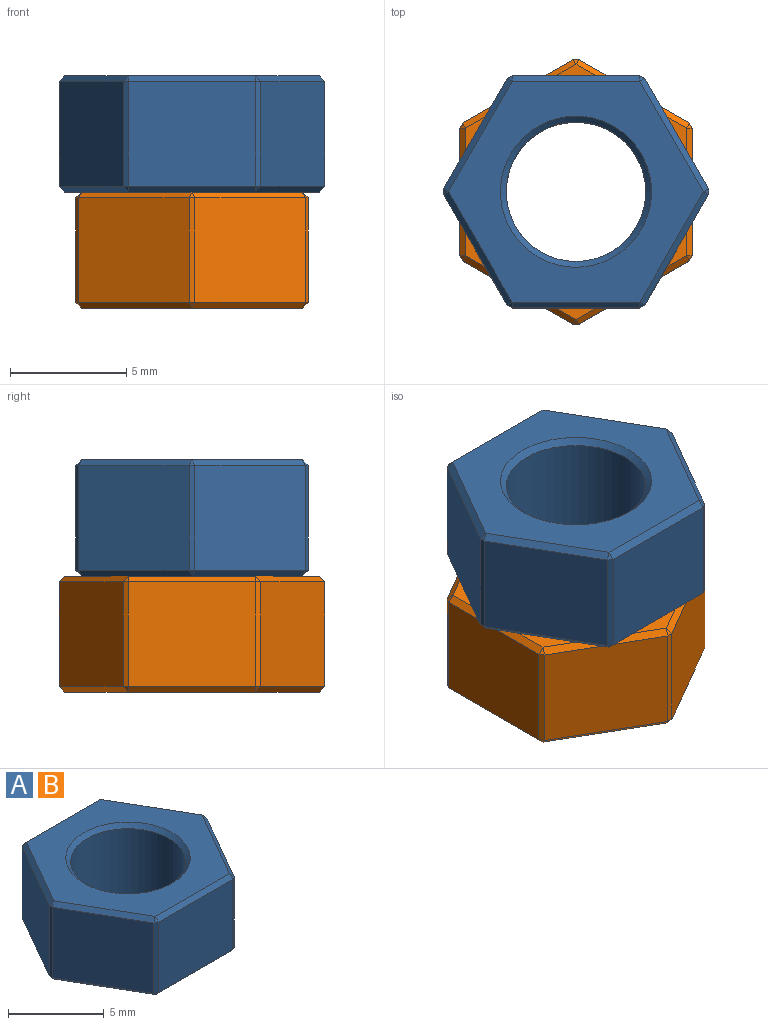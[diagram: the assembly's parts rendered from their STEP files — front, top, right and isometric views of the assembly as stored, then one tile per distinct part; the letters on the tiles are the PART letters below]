
ASSEMBLY  parts=2 mates=1
PART A: 40 faces, bbox 11.4x10x5 mm
  f0: plane 4.75x4.5mm, normal (-0.87,-0.5,0), area 24.7mm2, adj f15,f24,f25,f26
  f1: plane 5.49x4.5mm, normal (0,-1,0), area 24.7mm2, adj f10,f14,f15,f16
  f2: plane 4.75x4.5mm, normal (0.87,-0.5,0), area 24.7mm2, adj f10,f13,f17,f18
  f3: plane 4.75x4.5mm, normal (0.87,0.5,0), area 24.7mm2, adj f18,f23,f27,f28
  f4: plane 5.49x4.5mm, normal (0,1,0), area 24.7mm2, adj f28,f33,f36,f39
  f5: cylinder r=3mm len=6mm, axis (0,0,-1), area 89.5mm2, adj f8,f9
  f6: plane 4.75x4.5mm, normal (-0.87,0.5,0), area 24.7mm2, adj f25,f34,f35,f39
  f7: plane 10.97x9.5mm, normal (0,0,1), area 45mm2, adj f9,f13,f14,f23,f24,f33,f34
  f8: plane 10.97x9.5mm, normal (0,0,-1), area 49.9mm2, adj f5,f16,f17,f26,f27,f35,f36
  f9: cone r=3mm half-angle=45deg, axis (0,0,1), area 6.9mm2, adj f5,f7
  f10: plane 4.5x0.22mm, normal (0.5,-0.87,0), area 1.1mm2, adj f1,f2,f11,f12
  f11: plane 0.25x0.25mm, normal (0.38,-0.65,0.65), area 0mm2, adj f10,f13,f14
  f12: plane 0.25x0.25mm, normal (0.38,-0.65,-0.65), area 0mm2, adj f10,f16,f17
  f13: plane 4.88x2.96mm, normal (0.61,-0.35,0.71), area 1.9mm2, adj f2,f7,f11,f19
  f14: plane 5.49x0.25mm, normal (0,-0.71,0.71), area 1.9mm2, adj f1,f7,f11,f20
  f15: plane 4.5x0.22mm, normal (-0.5,-0.87,0), area 1.1mm2, adj f0,f1,f20,f21
  f16: plane 5.49x0.25mm, normal (0,-0.71,-0.71), area 1.9mm2, adj f1,f8,f12,f21
  f17: plane 4.88x2.96mm, normal (0.61,-0.35,-0.71), area 1.9mm2, adj f2,f8,f12,f22
  f18: plane 4.5x0.25mm, normal (1,0,0), area 1.1mm2, adj f2,f3,f19,f22
  f19: plane 0.25x0.25mm, normal (0.76,0,0.65), area 0mm2, adj f13,f18,f23
  f20: plane 0.25x0.25mm, normal (-0.38,-0.65,0.65), area 0mm2, adj f14,f15,f24
  f21: plane 0.25x0.25mm, normal (-0.38,-0.65,-0.65), area 0mm2, adj f15,f16,f26
  f22: plane 0.25x0.25mm, normal (0.76,0,-0.65), area 0mm2, adj f17,f18,f27
  f23: plane 4.88x2.96mm, normal (0.61,0.35,0.71), area 1.9mm2, adj f3,f7,f19,f29
  f24: plane 4.88x2.96mm, normal (-0.61,-0.35,0.71), area 1.9mm2, adj f0,f7,f20,f30
  f25: plane 4.5x0.25mm, normal (-1,0,0), area 1.1mm2, adj f0,f6,f30,f31
  f26: plane 4.88x2.96mm, normal (-0.61,-0.35,-0.71), area 1.9mm2, adj f0,f8,f21,f31
  f27: plane 4.88x2.96mm, normal (0.61,0.35,-0.71), area 1.9mm2, adj f3,f8,f22,f32
  f28: plane 4.5x0.22mm, normal (0.5,0.87,0), area 1.1mm2, adj f3,f4,f29,f32
  f29: plane 0.25x0.25mm, normal (0.38,0.65,0.65), area 0mm2, adj f23,f28,f33
  f30: plane 0.25x0.25mm, normal (-0.76,0,0.65), area 0mm2, adj f24,f25,f34
  f31: plane 0.25x0.25mm, normal (-0.76,0,-0.65), area 0mm2, adj f25,f26,f35
  f32: plane 0.25x0.25mm, normal (0.38,0.65,-0.65), area 0mm2, adj f27,f28,f36
  f33: plane 5.49x0.25mm, normal (0,0.71,0.71), area 1.9mm2, adj f4,f7,f29,f37
  f34: plane 4.88x2.96mm, normal (-0.61,0.35,0.71), area 1.9mm2, adj f6,f7,f30,f37
  f35: plane 4.88x2.96mm, normal (-0.61,0.35,-0.71), area 1.9mm2, adj f6,f8,f31,f38
  f36: plane 5.49x0.25mm, normal (0,0.71,-0.71), area 1.9mm2, adj f4,f8,f32,f38
  f37: plane 0.25x0.25mm, normal (-0.38,0.65,0.65), area 0mm2, adj f33,f34,f39
  f38: plane 0.25x0.25mm, normal (-0.38,0.65,-0.65), area 0mm2, adj f35,f36,f39
  f39: plane 4.5x0.22mm, normal (-0.5,0.87,0), area 1.1mm2, adj f4,f6,f37,f38
PART B: same geometry as A
PLACE A t=(3.53,-6.44,8.01)mm
PLACE B rot(axis=(0.71,-0.71,0),180deg) t=(3.53,-6.44,8.01)mm
MATE fastened B.f5 <-> A.f5  axis (0,0,1) through (3.53,-6.44,8.01)mm
